# Revit family: CurtainRail_90Deg_Nero_MeccaCare_1200mm
name_source: partatom
category: Specialty Equipment
units: mm (PartAtom-declared; Revit-internal decimal feet)

## family parameters
Always vertical = Yes
Cut with Voids When Loaded = Yes
Maintain Annotation Orientation = No
OmniClass Number = 23.31.17.31
OmniClass Title = Shower Rods
Part Type = Normal
Room Calculation Point = No
Round Connector Dimension = Use Diameter
Shared = No
Work Plane-Based = No

## types (6) — shared parameters
IfcExportAs = IfcFurnitureType
IfcExportType = USERDEFINED
Manufacturer = Nero
ManufacturerOverallDepth = 1211 mm  [stored 3.9731 ft]
ManufacturerOverallHeight = 1011 mm
ManufacturerOverallWidth = 1211 mm  [stored 3.9731 ft]
ManufacturerURLProductSpecific = https://nerotapware.com.au
ModifiedIssue = 20251105 $
URL = https://nerotapware.com.au
Uniclass2015Code = Pr_40_30_20_77
Uniclass2015Title = Shower curtain rails

## per-type parameters (varying)
| type | Assembly Code | Default Elevation | Description | ManufacturerSpecCode | Material | Model | Type Comments | Uniclass2015Version |
| Gunmetal (NRCR0006GM) | C1030210 | 1050 mm | Mecca Care Curtain Rail 1200x1200mm 90 Degree Gun Metal | NRCR0006GM | Metal_GunMetal_Nero | NRCR0006GM | Curtain Rail - 90 Deg - 1200mm - Gunmetal | Products v1.35 |
| Brushed Nickel (NRCR0006BN) | C1030210 | 1050 mm | Mecca Care Curtain Rail 1200x1200mm 90 Degree Brushed Nickel | NRCR0006BN | Metal_Nickel_Nero_Brushed | NRCR0006BN | Curtain Rail - 90 Deg - 1200mm - Brushed Nickel | Products v1.39 |
| Brushed Gold (NRCR0006BG) | C1030210 | 1050 mm | Mecca Care Curtain Rail 1200x1200mm 90 Degree Brushed Gold | NRCR0006BG | Metal_Gold_Nero_Brushed | NRCR0006BG | Curtain Rail - 90 Deg - 1200mm - Brushed Gold | Products v1.38 |
| Brushed Bronze (NRCR0006BZ) | C1030210 | 1050 mm | Mecca Care Curtain Rail 1200x1200mm 90 Degree Brushed Bronze | NRCR0006BZ | Metal_Bronze_Nero_Brushed | NRCR0006BZ | Curtain Rail - 90 Deg - 1200mm - Brushed Bronze | Products v1.37 |
| Matte Black (NRCR0006MB) | F1040 | 1050 mm | Mecca Care Curtain Rail 1200x1200mm 90 Degree Matte Black | NRCR0006MB | Metal_MatteBlack_Nero | NRCR0006MB | Curtain Rail - 90 Deg - 1200mm - Matte Black | Products v1.36 |
| Chrome (NRCR0006CH) | C1030210 | 2700 mm | Mecca Care Curtain Rail 1200x1200mm 90 Degree Chrome | NRCR0006CH | Metal_Chrome_Nero | NRCR0006CH | Curtain Rail - 90 Deg - 1200mm - Chrome | Products v1.35 |

note: [stored X ft] marks values corroborated as IEEE doubles in the binary element streams (Revit-internal decimal feet)

## geometry (parser evidence)
native form markers: Sweep x2
no freeform markers — native parametric forms only
